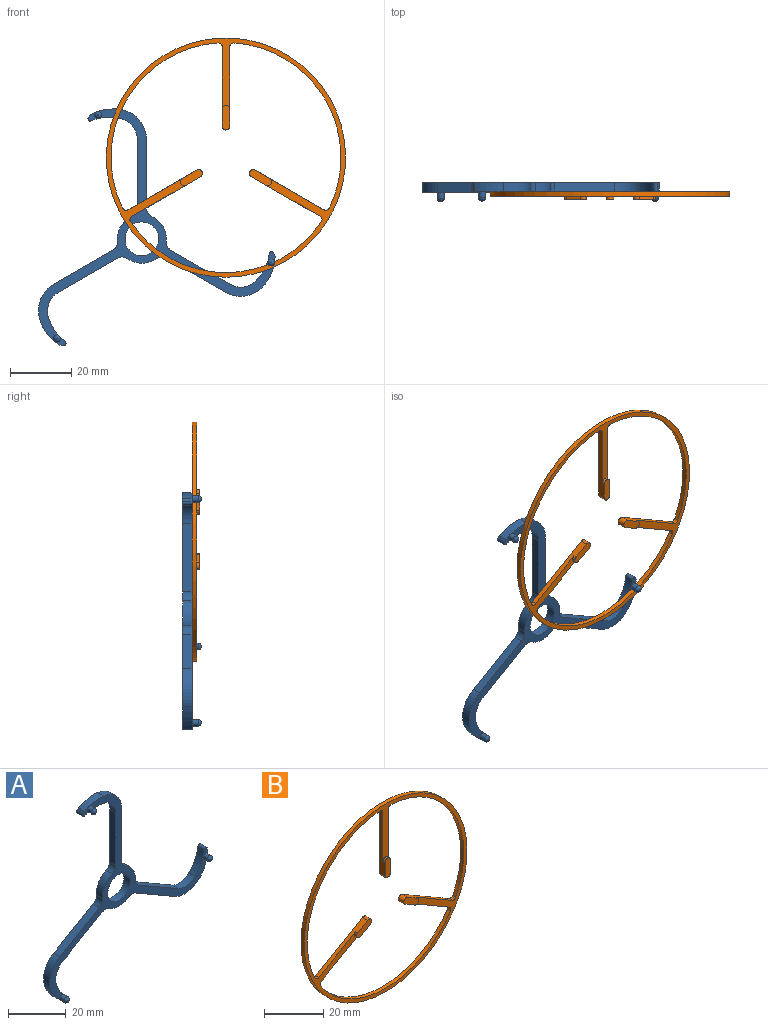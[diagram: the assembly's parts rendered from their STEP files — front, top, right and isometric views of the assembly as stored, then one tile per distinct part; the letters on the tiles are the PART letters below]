
ASSEMBLY  parts=2 mates=1
PART A: 48 faces, bbox 77.2x6x77.2 mm
  f0: plane 3.69x2.41mm, normal (0,-1,0), area 4.6mm2, adj f12,f13,f14,f25,f43
  f1: plane 76.92x75.78mm, normal (0,-1,0), area 488.1mm2, adj f3,f4,f5,f6,f8,f9,f10,f11
  f2: plane 3.75x3.07mm, normal (0,-1,0), area 4.6mm2, adj f6,f7,f8,f26,f41
  f3: plane 22.3x3mm, normal (-1,0,0), area 66.9mm2, adj f1,f23,f30,f33
  f4: cylinder r=8mm len=8.12mm, axis (0,1,0), area 30mm2, adj f1,f23,f33,f38
  f5: plane 19.27x11.13mm, normal (-0.5,0,0.87), area 66.8mm2, adj f1,f23,f29,f38
  f6: cylinder r=16mm len=7.37mm, axis (0,1,0), area 29.4mm2, adj f1,f2,f7,f23,f29
  f7: plane 3x1.13mm, normal (-0.13,0,-0.99), area 3.4mm2, adj f2,f6,f23,f26
  f8: cylinder r=15mm len=8.27mm, axis (0,1,0), area 30.4mm2, adj f1,f2,f23,f26,f32
  f9: plane 19.32x11.15mm, normal (0.5,0,-0.87), area 66.9mm2, adj f1,f23,f32,f37
  f10: cylinder r=8mm len=9.37mm, axis (0,1,0), area 30mm2, adj f1,f23,f36,f37
  f11: plane 19.27x11.13mm, normal (-0.5,0,-0.87), area 66.8mm2, adj f1,f23,f28,f36
  f12: cylinder r=16mm len=9.08mm, axis (0,1,0), area 29.4mm2, adj f0,f1,f13,f23,f28
  f13: plane 3x1.06mm, normal (0.92,0,0.38), area 3.4mm2, adj f0,f12,f23,f25
  f14: cylinder r=15mm len=8.91mm, axis (0,1,0), area 30.4mm2, adj f0,f1,f23,f25,f31
  f15: plane 19.32x11.15mm, normal (0.5,0,0.87), area 66.9mm2, adj f1,f23,f31,f35
  f16: cylinder r=8mm len=8.12mm, axis (0,1,0), area 30mm2, adj f1,f23,f34,f35
  f17: plane 22.26x3mm, normal (1,0,0), area 66.8mm2, adj f1,f23,f27,f34
  f18: cylinder r=16mm len=9.49mm, axis (0,1,0), area 29.4mm2, adj f1,f19,f22,f23,f27
  f19: plane 3x0.91mm, normal (-0.79,0,0.61), area 3.4mm2, adj f18,f22,f23,f24
  f20: cylinder r=15mm len=9.92mm, axis (0,1,0), area 30.4mm2, adj f1,f22,f23,f24,f30
  f21: cylinder r=5.5mm len=11mm, axis (0,1,0), area 103.7mm2, adj f1,f23
  f22: plane 3.49x3mm, normal (0,-1,0), area 4.6mm2, adj f18,f19,f20,f24,f39
  f23: plane 77.23x77.15mm, normal (0,1,0), area 513.6mm2, adj f3,f4,f5,f6,f7,f8,f9,f10
  f24: cylinder r=0.75mm len=3mm, axis (0,1,0), area 5.9mm2, adj f19,f20,f22,f23
  f25: cylinder r=0.75mm len=3mm, axis (0,1,0), area 5.9mm2, adj f0,f13,f14,f23
  f26: cylinder r=0.75mm len=3mm, axis (0,1,0), area 5.9mm2, adj f2,f7,f8,f23
  f27: cylinder r=10mm len=9.92mm, axis (0,1,0), area 43.3mm2, adj f1,f17,f18,f23
  f28: cylinder r=10mm len=12.95mm, axis (0,1,0), area 43.3mm2, adj f1,f11,f12,f23
  f29: cylinder r=10mm len=12.52mm, axis (0,1,0), area 43.3mm2, adj f1,f5,f6,f23
  f30: cylinder r=7mm len=6.74mm, axis (0,1,0), area 27.2mm2, adj f1,f3,f20,f23
  f31: cylinder r=7mm len=8.39mm, axis (0,1,0), area 27.2mm2, adj f1,f14,f15,f23
  f32: cylinder r=7mm len=7.79mm, axis (0,1,0), area 27.2mm2, adj f1,f8,f9,f23
  f33: cylinder r=3mm len=3mm, axis (0,1,0), area 10.3mm2, adj f1,f3,f4,f23
  f34: cylinder r=3mm len=3mm, axis (0,1,0), area 10.3mm2, adj f1,f16,f17,f23
  f35: cylinder r=3mm len=3mm, axis (0,1,0), area 10.3mm2, adj f1,f15,f16,f23
  f36: cylinder r=3mm len=3.26mm, axis (0,1,0), area 10.3mm2, adj f1,f10,f11,f23
  f37: cylinder r=3mm len=3.26mm, axis (0,1,0), area 10.3mm2, adj f1,f9,f10,f23
  f38: cylinder r=3mm len=3mm, axis (0,1,0), area 10.3mm2, adj f1,f4,f5,f23
  f39: cylinder r=1.12mm len=2.24mm, axis (0,1,0), area 14.1mm2, adj f1,f22,f47
  f40: plane 0.24x0.24mm, normal (0,-1,0), area 0mm2, adj f47
  f41: cylinder r=1.12mm len=2.24mm, axis (0,1,0), area 14.1mm2, adj f1,f2,f46
  f42: plane 0.24x0.24mm, normal (0,-1,0), area 0mm2, adj f46
  f43: cylinder r=1.12mm len=2.24mm, axis (0,1,0), area 14.1mm2, adj f0,f1,f45
  f44: plane 0.24x0.24mm, normal (0,-1,0), area 0mm2, adj f45
  f45: torus R=0.12mm, axis (0,-1,0), area 7.4mm2, adj f43,f44
  f46: torus R=0.12mm, axis (0,-1,0), area 7.4mm2, adj f41,f42
  f47: torus R=0.12mm, axis (0,-1,0), area 7.4mm2, adj f39,f40
PART B: 27 faces, bbox 78x2.5x78 mm
  f0: cylinder r=37.5mm len=53.88mm, axis (0,1,0), area 110mm2, adj f10,f11,f21,f26
  f1: plane 22.44x12.96mm, normal (0.5,0,0.87), area 44.4mm2, adj f10,f11,f14,f15,f16,f21
  f2: plane 22.44x12.96mm, normal (-0.5,0,-0.87), area 44.4mm2, adj f10,f11,f14,f15,f16,f22
  f3: cylinder r=37.5mm len=62.21mm, axis (0,1,0), area 110mm2, adj f10,f11,f22,f23
  f4: plane 22.44x12.96mm, normal (0.5,0,-0.87), area 44.4mm2, adj f10,f11,f13,f17,f18,f23
  f5: plane 22.44x12.96mm, normal (-0.5,0,0.87), area 44.4mm2, adj f10,f11,f13,f17,f18,f24
  f6: cylinder r=37.5mm len=53.88mm, axis (0,1,0), area 110mm2, adj f10,f11,f24,f25
  f7: plane 25.91x2.5mm, normal (-1,0,0), area 44.4mm2, adj f10,f11,f12,f19,f20,f25
  f8: plane 25.91x2.5mm, normal (1,0,0), area 44.4mm2, adj f10,f11,f12,f19,f20,f26
  f9: cylinder r=39mm len=78mm, axis (0,1,0), area 367.6mm2, adj f10,f11
  f10: plane 78x78mm, normal (0,-1,0), area 518.5mm2, adj f0,f1,f2,f3,f4,f5,f6,f7
  f11: plane 78x78mm, normal (0,1,0), area 574.5mm2, adj f0,f1,f2,f3,f4,f5,f6,f7
  f12: plane 8x2.5mm, normal (0,-1,0), area 18.7mm2, adj f7,f8,f19,f20
  f13: plane 7.26x5.25mm, normal (0,-1,0), area 18.7mm2, adj f4,f5,f17,f18
  f14: plane 7.26x5.25mm, normal (0,-1,0), area 18.7mm2, adj f1,f2,f15,f16
  f15: cylinder r=1.25mm len=2.33mm, axis (0,-1,0), area 3.9mm2, adj f1,f2,f10,f14
  f16: cylinder r=1.25mm len=2.5mm, axis (0,-1,0), area 9.8mm2, adj f1,f2,f11,f14
  f17: cylinder r=1.25mm len=2.33mm, axis (0,-1,0), area 3.9mm2, adj f4,f5,f10,f13
  f18: cylinder r=1.25mm len=2.5mm, axis (0,-1,0), area 9.8mm2, adj f4,f5,f11,f13
  f19: cylinder r=1.25mm len=2.5mm, axis (0,-1,0), area 3.9mm2, adj f7,f8,f10,f12
  f20: cylinder r=1.25mm len=2.5mm, axis (0,-1,0), area 9.8mm2, adj f7,f8,f11,f12
  f21: cylinder r=1.25mm len=1.75mm, axis (0,1,0), area 3.1mm2, adj f0,f1,f10,f11
  f22: cylinder r=1.25mm len=1.78mm, axis (0,1,0), area 3.1mm2, adj f2,f3,f10,f11
  f23: cylinder r=1.25mm len=1.78mm, axis (0,1,0), area 3.1mm2, adj f3,f4,f10,f11
  f24: cylinder r=1.25mm len=1.75mm, axis (0,1,0), area 3.1mm2, adj f5,f6,f10,f11
  f25: cylinder r=1.25mm len=1.5mm, axis (0,1,0), area 3.1mm2, adj f6,f7,f10,f11
  f26: cylinder r=1.25mm len=1.5mm, axis (0,1,0), area 3.1mm2, adj f0,f8,f10,f11
PLACE A t=(-35.32,-9.53,1.97)mm
PLACE B t=(-7.9,-12.53,28.43)mm
MATE fastened B.f11 <-> A.f1  axis (0,1,0) through (-38.59,-12.53,9.27)mm
